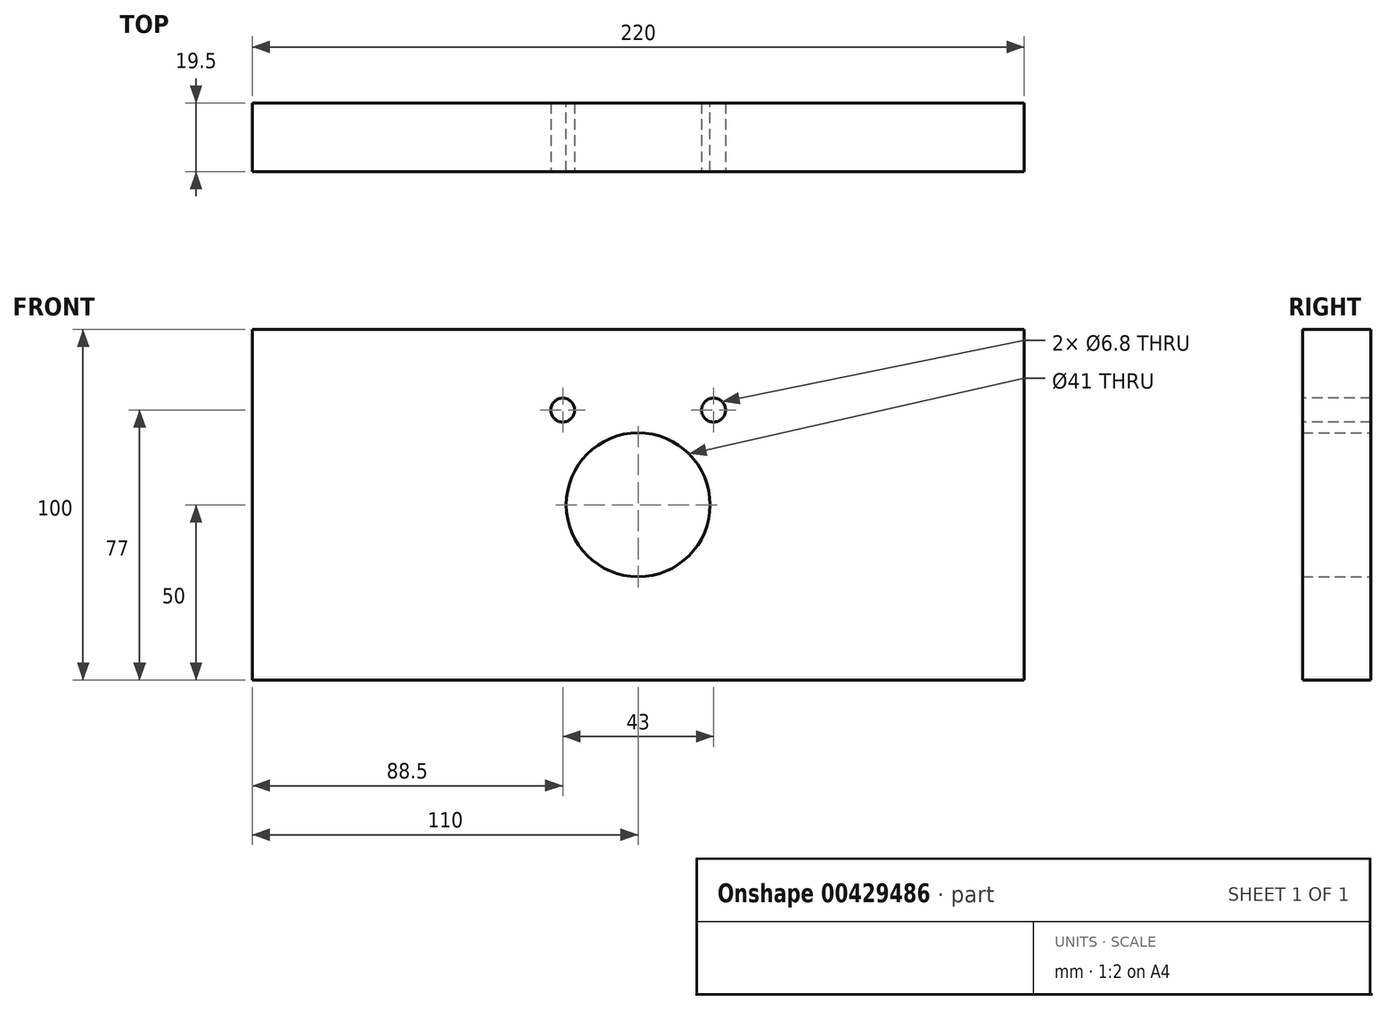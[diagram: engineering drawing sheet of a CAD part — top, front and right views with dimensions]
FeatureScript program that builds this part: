
annotation { "Feature Type Name" : "Feature", "Feature Type Description" : "" }
export const myFeature = defineFeature(function(context is Context, id is Id, definition is map)
    precondition{}
    {
        {
            var Q0;
            Q0=qCreatedBy(makeId("Front.planeOp"),FACE);
            var sketch = newSketch(context, id + "F0", { "sketchPlane" : qUnion([Q0])});
            skLineSegment(sketch, "E0.bottom", {"start": v(-110, 50) * mm, "end": v(110, 50) * mm});
            skLineSegment(sketch, "E0.top", {"start": v(-110, -50) * mm, "end": v(110, -50) * mm});
            skLineSegment(sketch, "E0.left", {"start": v(-110, 50) * mm, "end": v(-110, -50) * mm});
            skLineSegment(sketch, "E0.right", {"start": v(110, 50) * mm, "end": v(110, -50) * mm});
            skPoint(sketch, "E0.middle", {"position": v(0, 0) * mm});
            skCircle(sketch, "E1", {"center": v(0, 0) * mm, "radius": 20.5 * mm});
            skSolve(sketch);
        }
        {
            var Q0;
            Q0 = qSketchRegion(id + "F0", true);
            extrude(context, id + "F1", {"entities" : qUnion([Q0]), "depth" : 19.5 * mm});
        }
        {
            var Q0;
            Q0=makeQuery(id+"F1.opExtrude","CAP_FACE",FACE,{"disambiguationData":[OSD([sQuery(id+"F0.wireOp",EDGE,"E0.bottom"),sQuery(id+"F0.wireOp",EDGE,"E0.top"),sQuery(id+"F0.wireOp",EDGE,"E0.left"),sQuery(id+"F0.wireOp",EDGE,"E0.right"),sQuery(id+"F0.wireOp",EDGE,"E1")])],"isStart":false});
            var sketch = newSketch(context, id + "F2", { "sketchPlane" : qUnion([Q0])});
            skPoint(sketch, "E2", {"position": v(-21.5, 27) * mm});
            skPoint(sketch, "E3", {"position": v(21.5, 27) * mm});
            skSolve(sketch);
        }
        {
            var Q0;
            Q0=sQuery(id+"F2.wireOp",VERTEX,"E2");
            var Q1;
            Q1=sQuery(id+"F2.wireOp",VERTEX,"E3");
            var Q2;
            Q2=makeQuery(id+"F1.opExtrude","SWEPT_BODY",BODY,{"disambiguationData":[OSD([sQuery(id+"F0.wireOp",EDGE,"E0.bottom"),sQuery(id+"F0.wireOp",EDGE,"E0.top"),sQuery(id+"F0.wireOp",EDGE,"E0.left"),sQuery(id+"F0.wireOp",EDGE,"E0.right"),sQuery(id+"F0.wireOp",EDGE,"E1")])]});
            hole(context, id + "F3", {"style" : HoleStyle.SIMPLE, "endStyle" : HoleEndStyle.BLIND, "standardTappedOrClearance" : lookupTablePath({ "standard" : "ISO", "engagement" : "75%", "pitch" : "1.25 mm", "size" : "M8", "type" : "Tapped" }), "standardBlindInLast" : lookupTablePath({ "standard" : "ISO", "engagement" : "75%", "pitch" : "1.25 mm", "size" : "M8", "type" : "Tapped" }), "holeDiameter" : 6.8 * mm, "showTappedDepth" : true, "holeDepth" : 20 * mm, "isTappedThrough" : true, "tappedDepth" : 16.25 * mm, "tapClearance" : 3, "locations" : qUnion([Q0, Q1]), "scope" : qUnion([Q2]), "majorDiameter" : 8 * mm});
        }
    });
